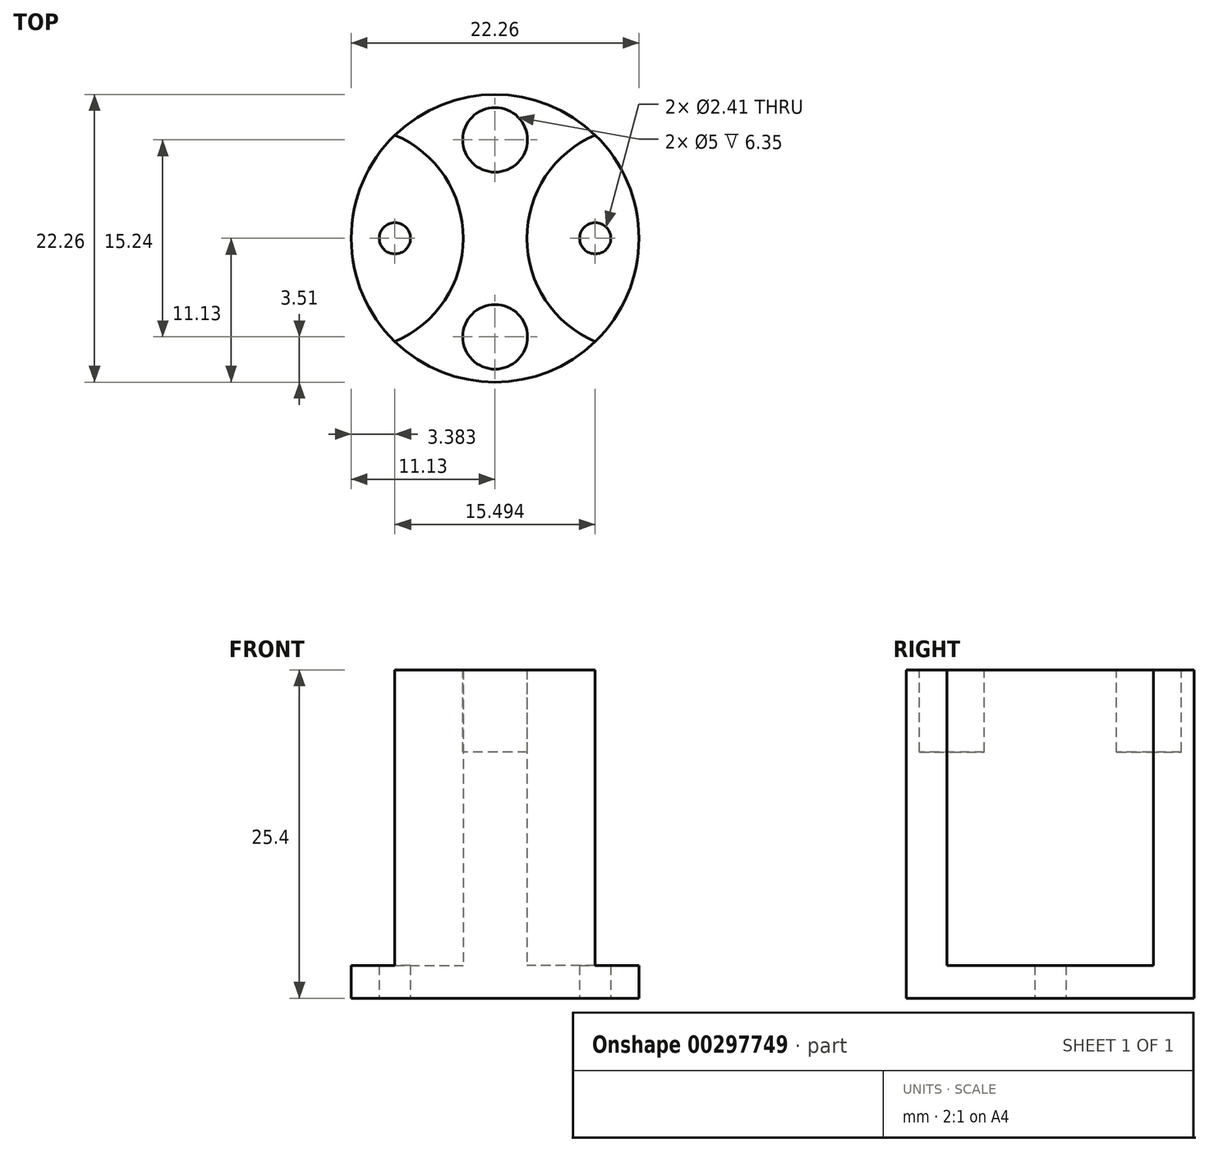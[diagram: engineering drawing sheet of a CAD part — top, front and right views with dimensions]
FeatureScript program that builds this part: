
annotation { "Feature Type Name" : "Feature", "Feature Type Description" : "" }
export const myFeature = defineFeature(function(context is Context, id is Id, definition is map)
    precondition{}
    {
        {
            var Q0;
            Q0=qCreatedBy(makeId("Top.planeOp"),FACE);
            var sketch = newSketch(context, id + "F0", { "sketchPlane" : qUnion([Q0])});
            skCircle(sketch, "E0", {"center": v(0, 0) * mm, "radius": 11.13 * mm});
            skLineSegment(sketch, "E1", {"start": v(-7.75, 0) * mm, "end": v(7.75, 0) * mm, "construction": true});
            skCircle(sketch, "E2", {"center": v(-7.75, 0) * mm, "radius": 1.2 * mm});
            skCircle(sketch, "E3", {"center": v(7.75, 0) * mm, "radius": 1.2 * mm});
            skArc(sketch, "E4", {"start": v(-7.75, -7.98) * mm, "mid": v(-2.46, 0) * mm, "end": v(-7.75, 7.98) * mm});
            skArc(sketch, "E5", {"start": v(7.75, 7.98) * mm, "mid": v(2.46, 0) * mm, "end": v(7.75, -7.98) * mm});
            skSolve(sketch);
        }
        {
            var Q0;
            Q0=makeQuery(id+"F0.imprint","IMPRINT",FACE,{"disambiguationData":[TD([[makeQuery(id+"F0.imprint","IMPRINT",EDGE,{"derivedFrom":sQuery(id+"F0.wireOp",EDGE,"E0")}),1.0]])]});
            var Q1;
            Q1=makeQuery(id+"F0.imprint","IMPRINT",FACE,{"disambiguationData":[TD([[makeQuery(id+"F0.imprint","IMPRINT",EDGE,{"derivedFrom":sQuery(id+"F0.wireOp",EDGE,"XoCQsdPc-5giJ-CtCa-5K4H-glQGGhhxyMcp")}),1.0]])]});
            var Q2;
            Q2=makeQuery(id+"F0.imprint","IMPRINT",FACE,{"disambiguationData":[TD([[makeQuery(id+"F0.imprint","IMPRINT",EDGE,{"derivedFrom":sQuery(id+"F0.wireOp",EDGE,"u1NtJBwG-5cgt-aVpu-KcLQ-YCcQKVe5bR7z")}),1.0]])]});
            var Q3;
            Q3=makeQuery(id+"F0.imprint","IMPRINT",FACE,{"disambiguationData":[TD([[makeQuery(id+"F0.imprint","IMPRINT",EDGE,{"derivedFrom":sQuery(id+"F0.wireOp",EDGE,"zNHpCZsX-YvX7-8d9m-vKEI-iuG1OG3aQ6j8")}),1.0]])]});
            var Q4;
            Q4=makeQuery(id+"F0.imprint","IMPRINT",FACE,{"disambiguationData":[TD([[makeQuery(id+"F0.imprint","IMPRINT",EDGE,{"derivedFrom":sQuery(id+"F0.wireOp",EDGE,"GcWkVqZg-JNaa-8IZR-hosm-SIRonIdEdPJH")}),1.0]])]});
            var Q5;
            Q5=makeQuery(id+"F0.imprint","IMPRINT",FACE,{"disambiguationData":[TD([[makeQuery(id+"F0.imprint","IMPRINT",EDGE,{"derivedFrom":sQuery(id+"F0.wireOp",EDGE,"E2")}),-1.0]])]});
            var Q6;
            Q6=makeQuery(id+"F0.imprint","IMPRINT",FACE,{"disambiguationData":[TD([[makeQuery(id+"F0.imprint","IMPRINT",EDGE,{"derivedFrom":sQuery(id+"F0.wireOp",EDGE,"E3")}),-1.0]])]});
            extrude(context, id + "F1", {"entities" : qUnion([Q0, Q1, Q2, Q3, Q4, Q5, Q6]), "depth" : 2.54 * mm});
        }
        {
            var Q0;
            Q0=makeQuery(id+"F1.opExtrude","CAP_FACE",FACE,{"disambiguationData":[OSD([sQuery(id+"F0.wireOp",EDGE,"E0"),sQuery(id+"F0.wireOp",EDGE,"E2"),sQuery(id+"F0.wireOp",EDGE,"E3")])],"isStart":false});
            var sketch = newSketch(context, id + "F2", { "sketchPlane" : qUnion([Q0])});
            skPoint(sketch, "E6", {"position": v(-7.75, 0) * mm});
            skPoint(sketch, "E7", {"position": v(7.75, 0) * mm});
            skArc(sketch, "E8", {"start": v(-7.75, -7.98) * mm, "mid": v(-2.46, 0) * mm, "end": v(-7.75, 7.98) * mm});
            skArc(sketch, "E9", {"start": v(7.75, 7.98) * mm, "mid": v(2.46, 0) * mm, "end": v(7.75, -7.98) * mm});
            skSolve(sketch);
        }
        {
            var Q0;
            {var subQ0=sQuery(id+"F2.wireOp",EDGE,"E8");Q0=makeQuery(id+"F2.imprint","IMPRINT",FACE,{"disambiguationData":[TD([[makeQuery(id+"F2.imprint","IMPRINT",EDGE,{"derivedFrom":subQ0}),-1.0]])]});}
            extrude(context, id + "F3", {"entities" : qUnion([Q0]), "operationType" : NewBodyOperationType.ADD, "depth" : 22.86 * mm});
        }
        {
            var Q0;
            Q0=makeQuery(id+"F3.opExtrude","CAP_FACE",FACE,{"disambiguationData":[OSD([sQuery(id+"F0.wireOp",EDGE,"E0"),sQuery(id+"F2.wireOp",EDGE,"E8"),sQuery(id+"F2.wireOp",EDGE,"E9")])],"isStart":false});
            var sketch = newSketch(context, id + "F4", { "sketchPlane" : qUnion([Q0])});
            skLineSegment(sketch, "E10", {"start": v(0, 7.62) * mm, "end": v(0, -7.62) * mm, "construction": true});
            skCircle(sketch, "E11", {"center": v(0, 7.62) * mm, "radius": 2.5 * mm});
            skCircle(sketch, "E12", {"center": v(0, -7.62) * mm, "radius": 2.5 * mm});
            skSolve(sketch);
        }
        {
            var Q0;
            Q0=makeQuery(id+"F4.imprint","IMPRINT",FACE,{"disambiguationData":[TD([[makeQuery(id+"F4.imprint","IMPRINT",EDGE,{"derivedFrom":sQuery(id+"F4.wireOp",EDGE,"E11")}),1.0]])]});
            var Q1;
            Q1=makeQuery(id+"F4.imprint","IMPRINT",FACE,{"disambiguationData":[TD([[makeQuery(id+"F4.imprint","IMPRINT",EDGE,{"derivedFrom":sQuery(id+"F4.wireOp",EDGE,"E12")}),1.0]])]});
            extrude(context, id + "F5", {"entities" : qUnion([Q0, Q1]), "operationType" : NewBodyOperationType.REMOVE, "oppositeDirection" : true, "depth" : 6.35 * mm});
        }
    });
